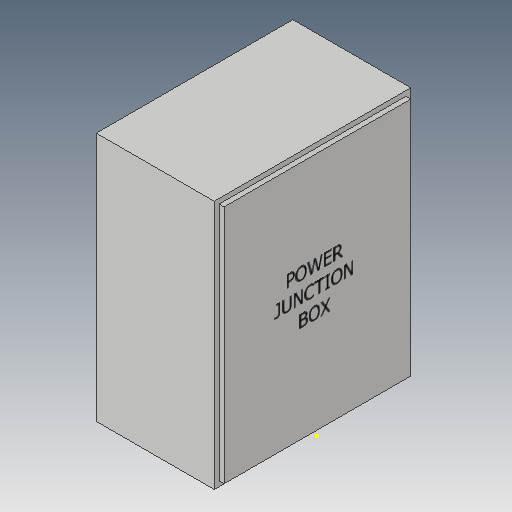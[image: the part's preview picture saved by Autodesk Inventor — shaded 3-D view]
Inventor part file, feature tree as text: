
AUTODESK INVENTOR PART (.ipt)
format: ipt  version: 2017 (Build 210142000, 142)  size: 112,128 bytes
history: native  units: in
note: dims shown in document units (in); Inventor stores cm internally (conversion verified against a paired STEP export)
features: sketch x5, extrude x3, shell x1
ambient origin geometry x8: Origin, YZ Plane, XZ Plane, XY Plane, X Axis, Y Axis, Z Axis, Center Point
bodies: Solid1 (feature_tree)
feature tree (9):
  extrude  "Extrusion1"  Depth=9.4488in
  sketch  "Sketch2"  dims[d4=1.9291in d5=1.9291in]
  sketch  "Sketch3"  dims[d6=7.874in d10=0.3937in]
  shell  "Shell1"  Thickness=20.0in
  extrude  "Extrusion2"  Depth=1.9291in
  extrude  "Extrusion3"  Depth=0.3937in
  sketch  "Sketch5"  dims[d13=0.3937in d14=0.0in d17=3.1228in d18=3.1228in]
  sketch  "Sketch1"  dims[d0=15.748in d1=9.4488in d2=20.0in d3=0.0in]
  sketch  "Sketch4"  dims[d11=0.3937in d12=0.0in]
